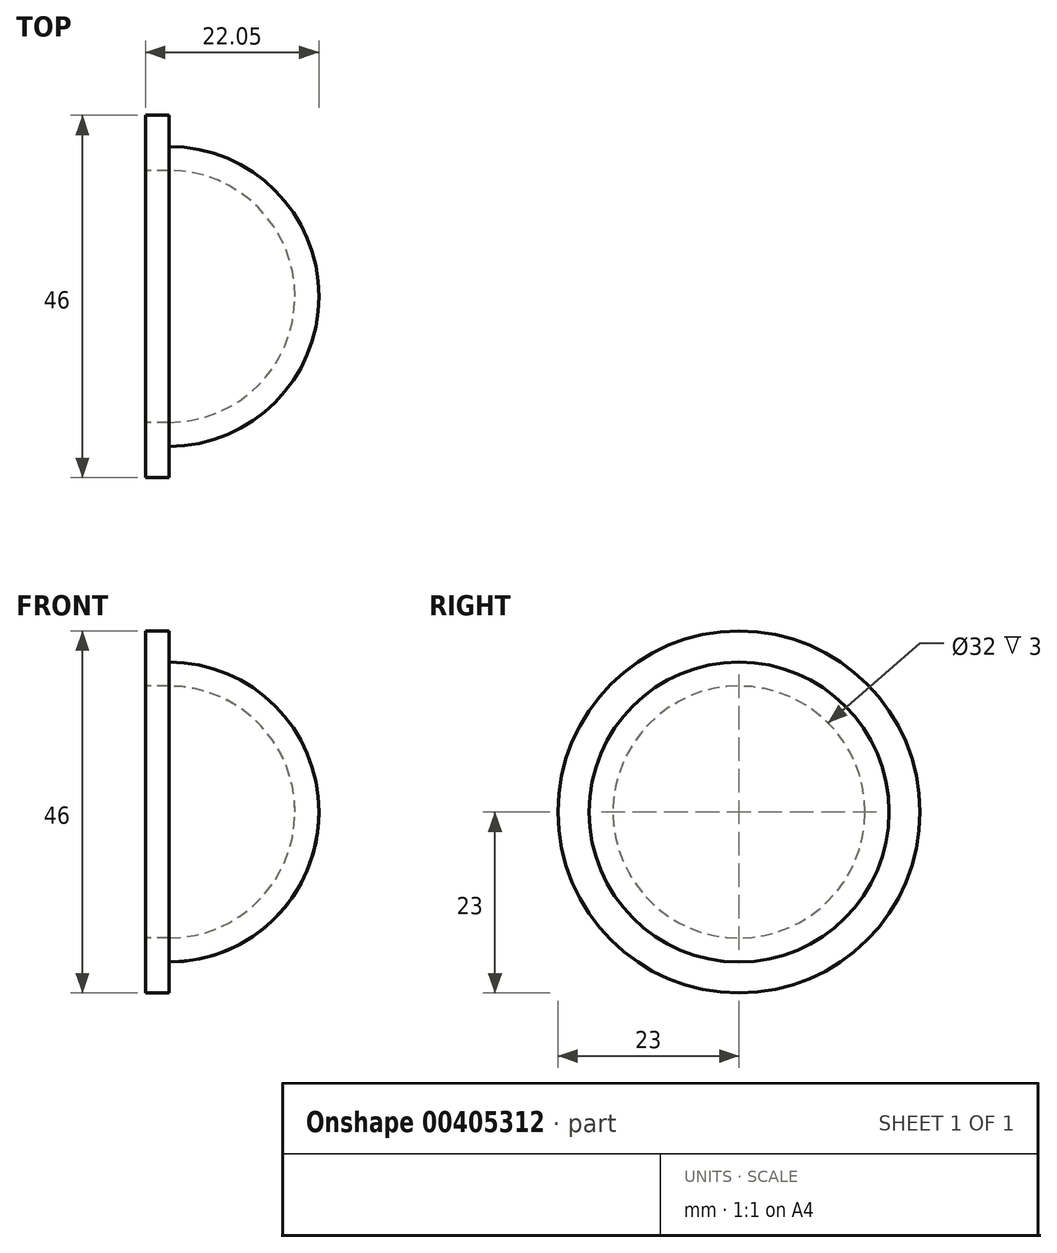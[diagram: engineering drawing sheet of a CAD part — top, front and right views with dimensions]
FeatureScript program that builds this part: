
annotation { "Feature Type Name" : "Feature", "Feature Type Description" : "" }
export const myFeature = defineFeature(function(context is Context, id is Id, definition is map)
    precondition{}
    {
        {
            var Q0;
            Q0=qCreatedBy(makeId("Front.planeOp"),FACE);
            var sketch = newSketch(context, id + "F0", { "sketchPlane" : qUnion([Q0])});
            skArc(sketch, "E0", {"start": v(19.05, 0) * mm, "mid": v(13.47, 13.47) * mm, "end": v(0, 19.05) * mm});
            skArc(sketch, "E1", {"start": v(16, 0) * mm, "mid": v(11.31, 11.31) * mm, "end": v(0, 16) * mm});
            skLineSegment(sketch, "E2", {"start": v(16, 0) * mm, "end": v(19.05, 0) * mm});
            skLineSegment(sketch, "E3.bottom", {"start": v(0, 16) * mm, "end": v(-3, 16) * mm});
            skLineSegment(sketch, "E3.top", {"start": v(0, 23) * mm, "end": v(-3, 23) * mm});
            skLineSegment(sketch, "E3.left", {"start": v(0, 19.05) * mm, "end": v(0, 23) * mm});
            skLineSegment(sketch, "E3.right", {"start": v(-3, 16) * mm, "end": v(-3, 23) * mm});
            skSolve(sketch);
        }
        {
            var Q0;
            Q0=makeQuery(id+"F0.imprint","IMPRINT",FACE,{"disambiguationData":[TD([[makeQuery(id+"F0.imprint","IMPRINT",EDGE,{"derivedFrom":sQuery(id+"F0.wireOp",EDGE,"E0")}),1.0]])]});
            var Q1;
            Q1=sQuery(id+"F0.wireOp",EDGE,"E2");
            revolve(context, id + "F1", {"entities" : qUnion([Q0]), "axis" : qUnion([Q1]), "revolveType" : RevolveType.FULL});
        }
    });
